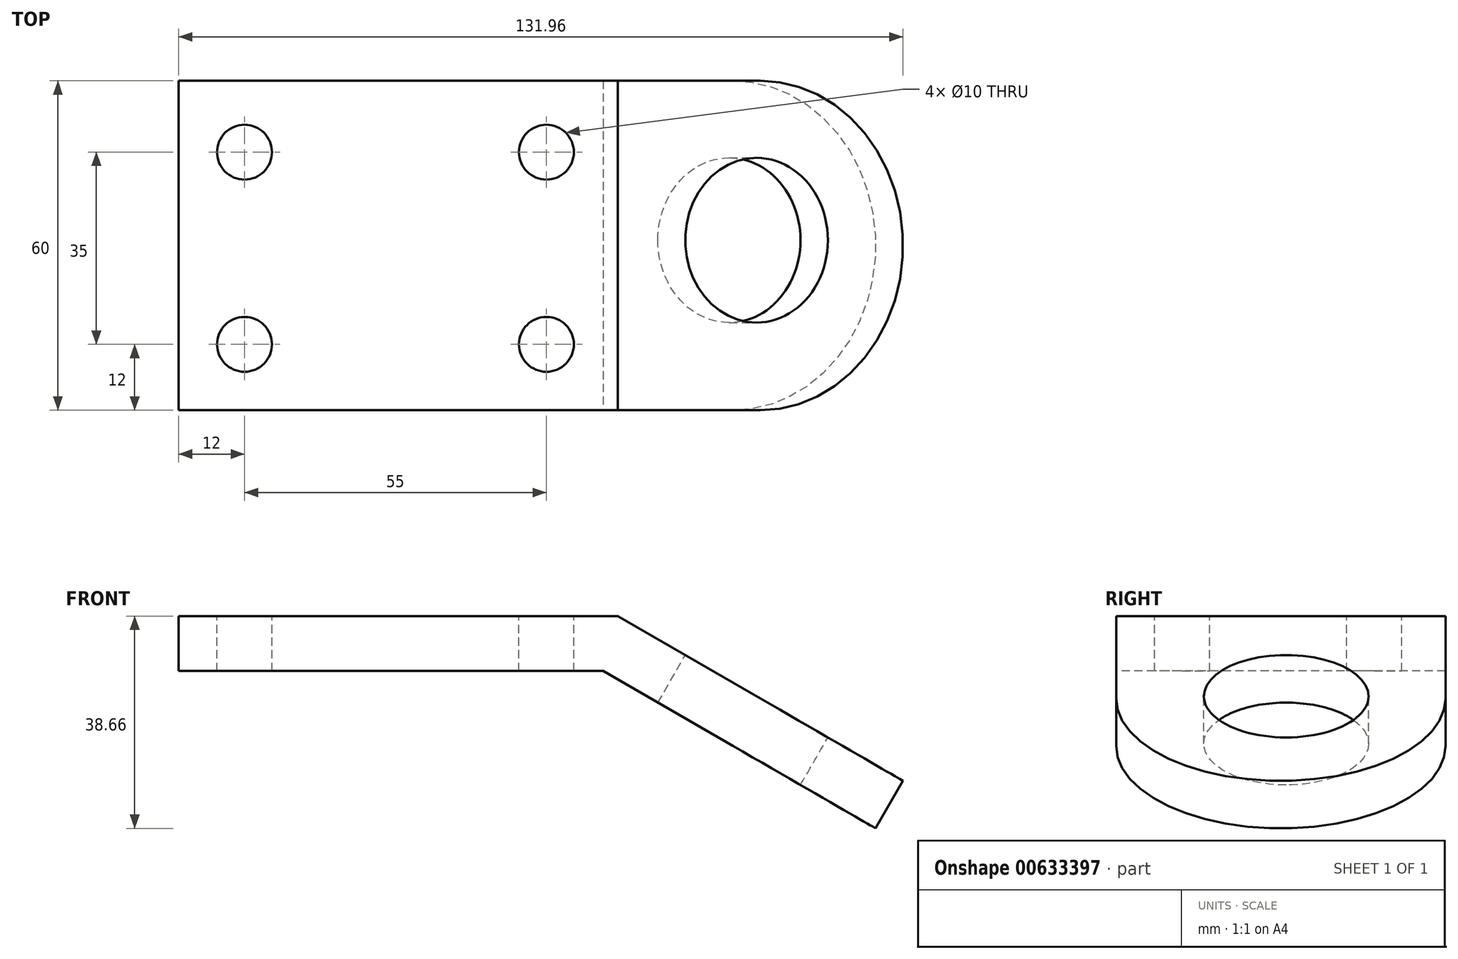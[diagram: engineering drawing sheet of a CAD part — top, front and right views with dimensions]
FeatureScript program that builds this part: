
annotation { "Feature Type Name" : "Feature", "Feature Type Description" : "" }
export const myFeature = defineFeature(function(context is Context, id is Id, definition is map)
    precondition{}
    {
        {
            var Q0;
            Q0=qCreatedBy(makeId("Front.planeOp"),FACE);
            var sketch = newSketch(context, id + "F0", { "sketchPlane" : qUnion([Q0])});
            skLineSegment(sketch, "E0", {"start": v(0, 0) * mm, "end": v(80, 0) * mm});
            skLineSegment(sketch, "E1", {"start": v(80, 0) * mm, "end": v(131.96, -30) * mm});
            skLineSegment(sketch, "E2.0", {"start": v(77.32, -10) * mm, "end": v(126.96, -38.66) * mm});
            skLineSegment(sketch, "E2.1", {"start": v(0, -10) * mm, "end": v(77.32, -10) * mm});
            skLineSegment(sketch, "E3", {"start": v(0, 0) * mm, "end": v(0, -10) * mm});
            skLineSegment(sketch, "E4", {"start": v(131.96, -30) * mm, "end": v(126.96, -38.66) * mm});
            skSolve(sketch);
        }
        {
            var Q0;
            Q0=makeQuery(id+"F0.imprint","IMPRINT",FACE,{"disambiguationData":[TD([[makeQuery(id+"F0.imprint","IMPRINT",EDGE,{"derivedFrom":sQuery(id+"F0.wireOp",EDGE,"E0")}),-1.0]])]});
            extrude(context, id + "F1", {"entities" : qUnion([Q0]), "oppositeDirection" : true, "depth" : 60 * mm, "offsetDistance" : 25 * mm});
        }
        {
            var Q0;
            Q0=makeQuery(id+"F1.opExtrude","CAP_EDGE",EDGE,{"disambiguationData":[OSD([sQuery(id+"F0.wireOp",EDGE,"E4")])],"isStart":false});
            var Q1;
            Q1=makeQuery(id+"F1.opExtrude","CAP_EDGE",EDGE,{"disambiguationData":[OSD([sQuery(id+"F0.wireOp",EDGE,"E4")])],"isStart":true});
            fillet(context, id + "F2", {"entities" : qUnion([Q0, Q1]), "radius" : 30 * mm, "tangentPropagation" : true, "allowEdgeOverflow" : false});
        }
        {
            var Q0;
            Q0=makeQuery(id+"F1.opExtrude","SWEPT_FACE",FACE,{"disambiguationData":[OSD([sQuery(id+"F0.wireOp",EDGE,"E1")])]});
            var sketch = newSketch(context, id + "F3", { "sketchPlane" : qUnion([Q0])});
            skCircle(sketch, "E5", {"center": v(98.48, 30.97) * mm, "radius": 15 * mm});
            skSolve(sketch);
        }
        {
            var Q0;
            Q0=makeQuery(id+"F3.imprint","IMPRINT",FACE,{"disambiguationData":[TD([[makeQuery(id+"F3.imprint","IMPRINT",EDGE,{"derivedFrom":sQuery(id+"F3.wireOp",EDGE,"E5")}),1.0]])]});
            extrude(context, id + "F4", {"entities" : qUnion([Q0]), "operationType" : NewBodyOperationType.REMOVE, "oppositeDirection" : true, "depth" : 78.3 * mm, "offsetDistance" : 25 * mm});
        }
        {
            var Q0;
            Q0=makeQuery(id+"F1.opExtrude","SWEPT_FACE",FACE,{"disambiguationData":[OSD([sQuery(id+"F0.wireOp",EDGE,"E0")])]});
            var sketch = newSketch(context, id + "F5", { "sketchPlane" : qUnion([Q0])});
            skCircle(sketch, "E6", {"center": v(12, 12) * mm, "radius": 5 * mm});
            skCircle(sketch, "E7.0.1.0", {"center": v(12, 47) * mm, "radius": 5 * mm});
            skCircle(sketch, "E7.1.0.0", {"center": v(67, 12) * mm, "radius": 5 * mm});
            skCircle(sketch, "E7.1.1.0", {"center": v(67, 47) * mm, "radius": 5 * mm});
            skLineSegment(sketch, "E7.direction1", {"start": v(12, 12) * mm, "end": v(67, 12) * mm, "construction": true});
            skLineSegment(sketch, "E7.direction2", {"start": v(12, 12) * mm, "end": v(12, 47) * mm, "construction": true});
            skSolve(sketch);
        }
        {
            var Q0;
            Q0=makeQuery(id+"F5.imprint","IMPRINT",FACE,{"disambiguationData":[TD([[makeQuery(id+"F5.imprint","IMPRINT",EDGE,{"derivedFrom":sQuery(id+"F5.wireOp",EDGE,"E7.0.1.0")}),1.0]])]});
            var Q1;
            Q1=makeQuery(id+"F5.imprint","IMPRINT",FACE,{"disambiguationData":[TD([[makeQuery(id+"F5.imprint","IMPRINT",EDGE,{"derivedFrom":sQuery(id+"F5.wireOp",EDGE,"E6")}),1.0]])]});
            var Q2;
            Q2=makeQuery(id+"F5.imprint","IMPRINT",FACE,{"disambiguationData":[TD([[makeQuery(id+"F5.imprint","IMPRINT",EDGE,{"derivedFrom":sQuery(id+"F5.wireOp",EDGE,"E7.1.0.0")}),1.0]])]});
            var Q3;
            Q3=makeQuery(id+"F5.imprint","IMPRINT",FACE,{"disambiguationData":[TD([[makeQuery(id+"F5.imprint","IMPRINT",EDGE,{"derivedFrom":sQuery(id+"F5.wireOp",EDGE,"E7.1.1.0")}),1.0]])]});
            extrude(context, id + "F6", {"entities" : qUnion([Q0, Q1, Q2, Q3]), "operationType" : NewBodyOperationType.REMOVE, "oppositeDirection" : true, "depth" : 25 * mm, "offsetDistance" : 25 * mm});
        }
    });
